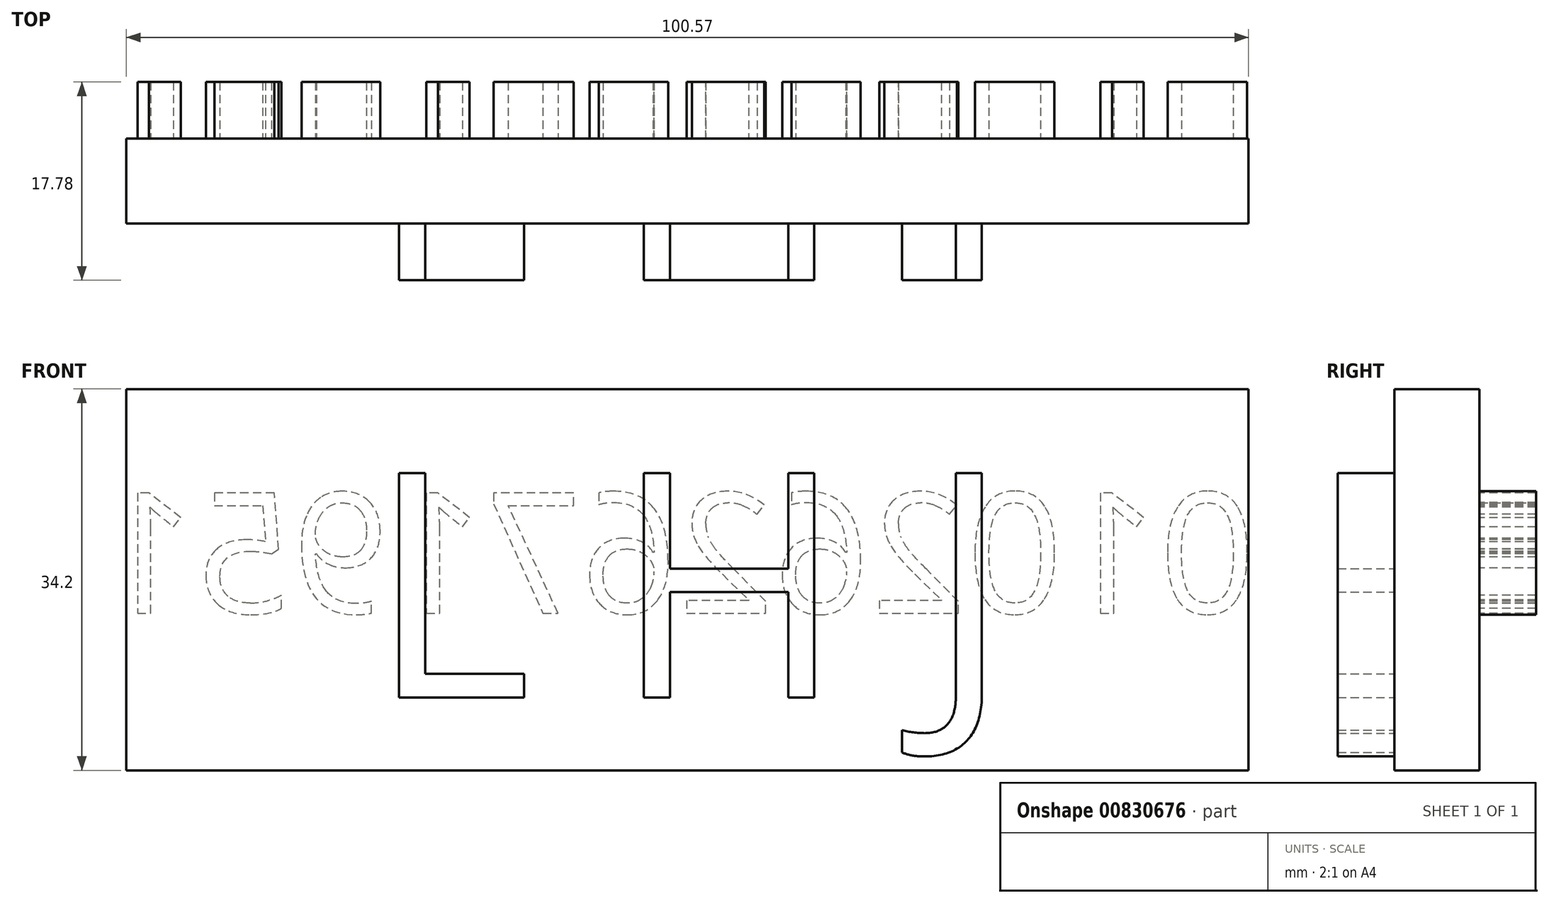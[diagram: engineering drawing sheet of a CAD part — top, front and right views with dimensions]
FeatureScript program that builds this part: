
annotation { "Feature Type Name" : "Feature", "Feature Type Description" : "" }
export const myFeature = defineFeature(function(context is Context, id is Id, definition is map)
    precondition{}
    {
        {
            var Q0;
            Q0=qCreatedBy(makeId("Front.planeOp"),FACE);
            var sketch = newSketch(context, id + "F0", { "sketchPlane" : qUnion([Q0])});
            skLineSegment(sketch, "E0.bottom", {"start": v(0, 0) * mm, "end": v(100.57, 0) * mm});
            skLineSegment(sketch, "E0.top", {"start": v(0, 34.2) * mm, "end": v(100.57, 34.2) * mm});
            skLineSegment(sketch, "E0.left", {"start": v(0, 0) * mm, "end": v(0, 34.2) * mm});
            skLineSegment(sketch, "E0.right", {"start": v(100.57, 0) * mm, "end": v(100.57, 34.2) * mm});
            skSolve(sketch);
        }
        {
            var Q0;
            Q0=makeQuery(id+"F0.imprint","IMPRINT",FACE,{"disambiguationData":[TD([[makeQuery(id+"F0.imprint","IMPRINT",EDGE,{"derivedFrom":sQuery(id+"F0.wireOp",EDGE,"E0.bottom")}),1.0]])]});
            extrude(context, id + "F1", {"entities" : qUnion([Q0]), "depth" : 7.62 * mm, "offsetDistance" : 25.4 * mm});
        }
        {
            var Q0;
            Q0=makeQuery(id+"F1.opExtrude","CAP_FACE",FACE,{"disambiguationData":[OSD([sQuery(id+"F0.wireOp",EDGE,"E0.bottom"),sQuery(id+"F0.wireOp",EDGE,"E0.top"),sQuery(id+"F0.wireOp",EDGE,"E0.left"),sQuery(id+"F0.wireOp",EDGE,"E0.right")])],"isStart":false});
            var sketch = newSketch(context, id + "F2", { "sketchPlane" : qUnion([Q0])});
            skText(sketch, "E1", { "text": "L H J", "fontName": "OpenSans-Regular.ttf"});
            const initialGuessF2  = {"E1": [0.02168, 0.00654, 1, 0, 0.02028]};
            skSetInitialGuess(sketch, initialGuessF2);
            skSolve(sketch);
        }
        {
            var Q0;
            Q0 = qSketchRegion(id + "F2", true);
            extrude(context, id + "F3", {"entities" : qUnion([Q0]), "operationType" : NewBodyOperationType.ADD, "depth" : 5.08 * mm, "offsetDistance" : 25.4 * mm});
        }
        {
            var Q0;
            Q0=makeQuery(id+"F1.opExtrude","CAP_FACE",FACE,{"disambiguationData":[OSD([sQuery(id+"F0.wireOp",EDGE,"E0.bottom"),sQuery(id+"F0.wireOp",EDGE,"E0.top"),sQuery(id+"F0.wireOp",EDGE,"E0.left"),sQuery(id+"F0.wireOp",EDGE,"E0.right")])],"isStart":true});
            var sketch = newSketch(context, id + "F4", { "sketchPlane" : qUnion([Q0])});
            skText(sketch, "E2", { "text": "010262671951", "fontName": "OpenSans-Regular.ttf"});
            const initialGuessF4  = {"E2": [-0.1012, 0.0141, 1, 0, 0.01087]};
            skSetInitialGuess(sketch, initialGuessF4);
            skSolve(sketch);
        }
        {
            var Q0;
            Q0 = qSketchRegion(id + "F4", true);
            extrude(context, id + "F5", {"entities" : qUnion([Q0]), "operationType" : NewBodyOperationType.ADD, "depth" : 5.08 * mm, "offsetDistance" : 25.4 * mm});
        }
    });
